# Revit family: LAMP_KOMBIC 150 SURFACE 3000 CRI80 OPAL
name_source: partatom
category: Luminarias
revit_build: Autodesk Revit 2018 (Build: 20190510_1515(x64)
units: mm (PartAtom-declared; Revit-internal decimal feet)

## family parameters
Anfitrión = Cara
Compartido = No
Corte con vacíos al cargar = No
Cota de conector redondo = Diámetro de uso
Origen de luz = Sí
Punto de cálculo de habitación = No
Tipo de pieza = Normal

## types (12) — shared parameters
CRI = 80
Cambio de temperatura de color de luz atenuada = <Ninguno>
Diameter = 150 mm
Elevación por defecto = 1219 mm
Fabricante = LAMP
Filtro de color = 16777215
Gear = Electronic
Height = 180 mm  [stored 0.590551 ft]
IEE = A+
Installation instructions = https://www.lamp.es
Insulation class = II
LED Lifetime = 50.000 L80 B10
Lamp = COB LED
Last update = 02/09/2021
Luminaire type = Suspended
MacAdam = 3
Manufacturer URL = http://www.lamp.es
Manufacturer country = Spain
Manufacturer name = LAMP
Material cable suspension = LAMP_Acero genérico
Material difusor = LAMP_PMMA Difusor Kombic
Model explanation = Possibility of chossing between surface or suspended within the model
Plum = 20 W
Power = 18 W
Power Supply = 220-240V 50/60Hz
Product URL = https://www.lamp.es
Product datasheet = http://www.lamp.es
Protection rating = IP40
Type = COB PHILIPS
Weight = 1.48 kg
Ángulo de inclinación = -90.00°

## per-type parameters (varying)
| type | Archivo de red fotométrica | Efficacy | Finish | Material cuerpo | Material floron | Material reflector | Modelo | Product code |
| 2010LM 3000K  M/B | K21SF3040OP830NMB.IES | 102 lm/W | Matte black RAL 9011 | LAMP_Plástico genérico NG | LAMP_Plástico genérico NG | LAMP_PC Reflector Kombic Metalizado Mate | K21SF3040OP830NMB | K21SF3040OP830NMB |
| 2010LM 3000K  M/W | K21SF3040OP830NMW.IES | 102 lm/W | Matte white RAL 9010 | LAMP_Plástico genérico BL | LAMP_Plástico genérico BL | LAMP_PC Reflector Kombic Metalizado Mate | K21SF3040OP830NMW | K21SF3040OP830NMW |
| 2074LM 3000K  W/B | K21SF3040OP830NWB.IES | 105 lm/W | Matte black RAL 9011 | LAMP_Plástico genérico NG | LAMP_Plástico genérico NG | LAMP_PC Reflector Kombic Blanco | K21SF3040OP830NWB | K21SF3040OP830NWB |
| 2074LM 3000K  W/W | K21SF3040OP830NWW.IES | 105 lm/W | Matte white RAL 9010 | LAMP_Plástico genérico BL | LAMP_Plástico genérico BL | LAMP_PC Reflector Kombic Blanco | K21SF3040OP830NWW | K21SF3040OP830NWW |
| 2094LM 4000K  M/B | K21SF3040OP840NMB.IES | 106 lm/W | Matte black RAL 9011 | LAMP_Plástico genérico NG | LAMP_Plástico genérico NG | LAMP_PC Reflector Kombic Metalizado Mate | K21SF3040OP840NMB | K21SF3040OP840NMB |
| 2094LM 4000K  M/W | K21SF3040OP840NMW.IES | 106 lm/W | Matte white RAL 9010 | LAMP_Plástico genérico BL | LAMP_Plástico genérico BL | LAMP_PC Reflector Kombic Metalizado Mate | K21SF3040OP840NMW | K21SF3040OP840NMW |
| 2096LM 3000K  BR/B | K21SF3040OP830NRB.IES | 106 lm/W | Matte black RAL 9011 | LAMP_Plástico genérico NG | LAMP_Plástico genérico NG | LAMP_PC Reflector Kombic Metalizado Brillante | K21SF3040OP830NRB | K21SF3040OP830NRB |
| 2096LM 3000K  BR/W | K21SF3040OP830NRW.IES | 106 lm/W | Matte white RAL 9010 | LAMP_Plástico genérico BL | LAMP_Plástico genérico BL | LAMP_PC Reflector Kombic Metalizado Brillante | K21SF3040OP830NRW | K21SF3040OP830NRW |
| 2161LM 4000K  W/B | K21SF3040OP840NWB.IES | 109 lm/W | Matte black RAL 9011 | LAMP_Plástico genérico NG | LAMP_Plástico genérico NG | LAMP_PC Reflector Kombic Blanco | K21SF3040OP840NWB | K21SF3040OP840NWB |
| 2161LM 4000K  W/W | K21SF3040OP840NWW.IES | 109 lm/W | Matte white RAL 9010 | LAMP_Plástico genérico BL | LAMP_Plástico genérico BL | LAMP_PC Reflector Kombic Blanco | K21SF3040OP840NWW | K21SF3040OP840NWW |
| 2184LM 4000K  BR/B | K21SF3040OP840NRB.IES | 110 lm/W | Matte black RAL 9011 | LAMP_Plástico genérico NG | LAMP_Plástico genérico NG | LAMP_PC Reflector Kombic Metalizado Brillante | K21SF3040OP840NRB | K21SF3040OP840NRB |
| 2184LM 4000K  BR/W | K21SF3040OP840NRW.IES | 110 lm/W | Matte white RAL 9010 | LAMP_Plástico genérico BL | LAMP_Plástico genérico BL | LAMP_PC Reflector Kombic Metalizado Brillante | K21SF3040OP840NRW | K21SF3040OP840NRW |

note: [stored X ft] marks values corroborated as IEEE doubles in the binary element streams (Revit-internal decimal feet)
